# Revit family: Lighting-Linear-Ledalite-Modifly-Quad_Link NEW
name_source: partatom
category: Lighting Fixtures
revit_build: Autodesk Revit 2017 (Build: 20160720_1515(x64)
units: mm (PartAtom-declared; Revit-internal decimal feet)

## family parameters
Cut with Voids When Loaded = No
Host = Face
Light Source = No
OmniClass Number = 23.80.70.11
OmniClass Title = Luminaries for Internal Lighting
Part Type = Normal
Room Calculation Point = No
Round Connector Dimension = Use Diameter
Shared = No

## types (1)
- Quad-Link
    Apparent Load = 0 W
    Available Finishes = Standard White, Halo Gold, Silver Nova, Venom Black, Titanium Silver, Black, Custom
    Cable Material Finish = Steel-Signify-Galvanized
    Catalog Number = Quad-Link
    Default Elevation = 0' - 0"
    Description = ModiFly Articulating Links
    Driver Comment = Contact Signify for Driver Options
    Fixture Material Finish = Plastic-Signify-White
    Frequency = 60 Hz
    Height = 0' - 4 123/256"
    Last Updated = 4.11.19
    Length = 0' - 3 41/256"
    Load Classification = Lighting
    Manufacturer = Ledalite
    Model = Quad-Link
    Mounting Method = Tamper-resistant aircraft cable gripper provides unlimited vertical adjustment.
Aircraft cable, crimp and cable gripper are independently tested to meet stringent safety requirements.
    Number of Poles = 1
    Phase = 1
    Power Factor = 1
    Product Documentation Link = Contact Signify for Product Documentation
    Product Family = ModiFly Articulating Links
    Product Page URL = http://www.lightingproducts.signify.com
    URL = https://www.signify.com
    Version = 2017 v1.0a
    Voltage = 120 V
    Voltage Comments = UNV120-277V, Low Voltage 48-54V DC, 347V
    Width = 0' - 2 59/128"
    eCatalog URL = www.ledalite.com

## geometry (parser evidence)
native form markers: Sweep x4
no freeform markers — native parametric forms only
